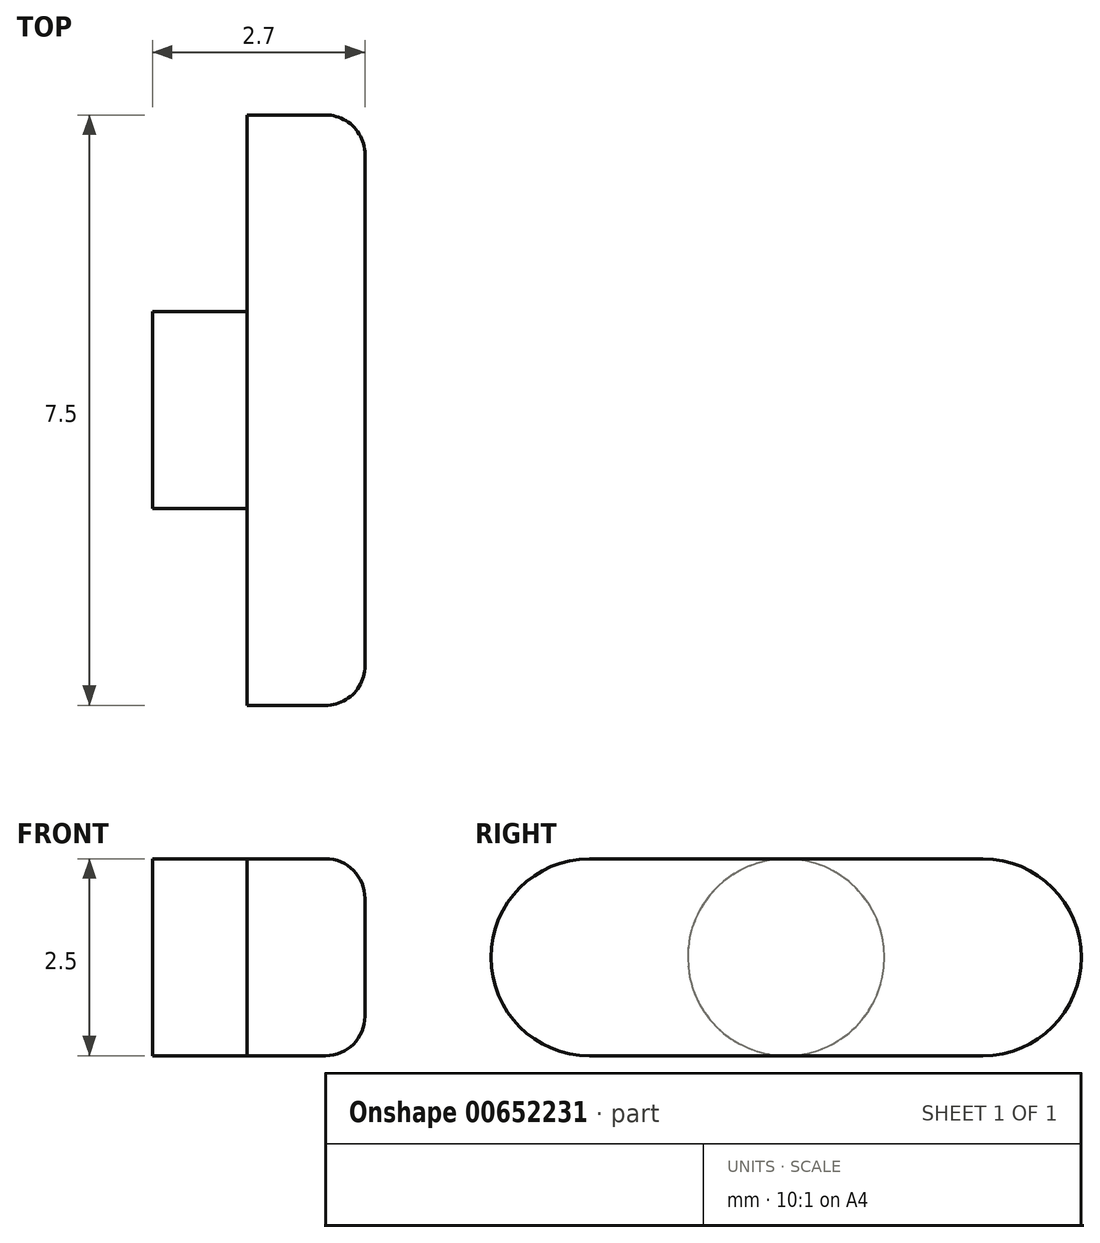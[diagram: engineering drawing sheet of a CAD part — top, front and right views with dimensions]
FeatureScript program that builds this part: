
annotation { "Feature Type Name" : "Feature", "Feature Type Description" : "" }
export const myFeature = defineFeature(function(context is Context, id is Id, definition is map)
    precondition{}
    {
        {
            var Q0;
            Q0=qCreatedBy(makeId("Right.planeOp"),FACE);
            var sketch = newSketch(context, id + "F0", { "sketchPlane" : qUnion([Q0])});
            skLineSegment(sketch, "E0.bottom", {"start": v(-2.5, 1.25) * mm, "end": v(2.5, 1.25) * mm});
            skLineSegment(sketch, "E0.top", {"start": v(-2.5, -1.25) * mm, "end": v(2.5, -1.25) * mm});
            skPoint(sketch, "E0.middle", {"position": v(0, 0) * mm});
            skArc(sketch, "E1", {"start": v(2.5, -1.25) * mm, "mid": v(3.75, 0) * mm, "end": v(2.5, 1.25) * mm});
            skArc(sketch, "E2", {"start": v(-2.5, 1.25) * mm, "mid": v(-3.75, 0) * mm, "end": v(-2.5, -1.25) * mm});
            skSolve(sketch);
        }
        {
            var Q0;
            Q0=qSketchRegion(id+"F0",true);
            extrude(context, id + "F1", {"entities" : qUnion([Q0]), "endBound" : BoundingType.SYMMETRIC, "depth" : 1.5 * mm, "offsetDistance" : 25 * mm});
        }
        {
            var Q0;
            Q0=makeQuery(id+"F1.opExtrude","CAP_FACE",FACE,{"disambiguationData":[OSD([sQuery(id+"F0.wireOp",EDGE,"E0.bottom"),sQuery(id+"F0.wireOp",EDGE,"E0.top"),sQuery(id+"F0.wireOp",EDGE,"E1"),sQuery(id+"F0.wireOp",EDGE,"E2")])],"isStart":false});
            fillet(context, id + "F2", {"entities" : qUnion([Q0]), "radius" : 0.5 * mm, "tangentPropagation" : true, "allowEdgeOverflow" : false});
        }
        {
            var Q0;
            Q0=makeQuery(id+"F1.opExtrude","CAP_FACE",FACE,{"disambiguationData":[OSD([sQuery(id+"F0.wireOp",EDGE,"E0.bottom"),sQuery(id+"F0.wireOp",EDGE,"E0.top"),sQuery(id+"F0.wireOp",EDGE,"E1"),sQuery(id+"F0.wireOp",EDGE,"E2")])],"isStart":true});
            var sketch = newSketch(context, id + "F3", { "sketchPlane" : qUnion([Q0])});
            skCircle(sketch, "E3", {"center": v(0, 0) * mm, "radius": 1.25 * mm});
            skSolve(sketch);
        }
        {
            var Q0;
            Q0=qSketchRegion(id+"F3",true);
            extrude(context, id + "F4", {"entities" : qUnion([Q0]), "operationType" : NewBodyOperationType.ADD, "depth" : 1.2 * mm, "offsetDistance" : 25 * mm});
        }
    });
